# Revit family: Clarity16C-Shaftway-Same-Side
name_source: partatom
category: Specialty Equipment
units: mm (PartAtom-declared; Revit-internal decimal feet)

## family parameters
Always vertical = Yes
Classification Number = 23.50.05.14.17.11
Cut with Voids When Loaded = No
Enable Cutting in Views = No
Maintain Annotation Orientation = No
Part Type = Normal
Room Calculation Point = No
Round Connector Dimension = Use Diameter
Shared = Yes
Work Plane-Based = No

## types (1)
- 16E
    Assembly Code = D1010310
    Brushes = Clarity_16E_Brushes
    Default Elevation = 0 "
    Description = Vertical platform wheelchair lift
    Keynote = 14400
    Length = 67.5 "
    MEP Apparent Power = 720 VA
    Manufacturer = Ascension, a division of AGM
    Model = Clarity 16C
    Powder Coated = Clarity_16E_Powdercoat
    Stainless = Clarity_16E_Stainless
    URL = ascension-lift.com
    Voltage_MEP = 120 V
    Width = 48.5 "

## geometry (parser evidence)
native form markers: Sweep x8
no freeform markers — native parametric forms only
